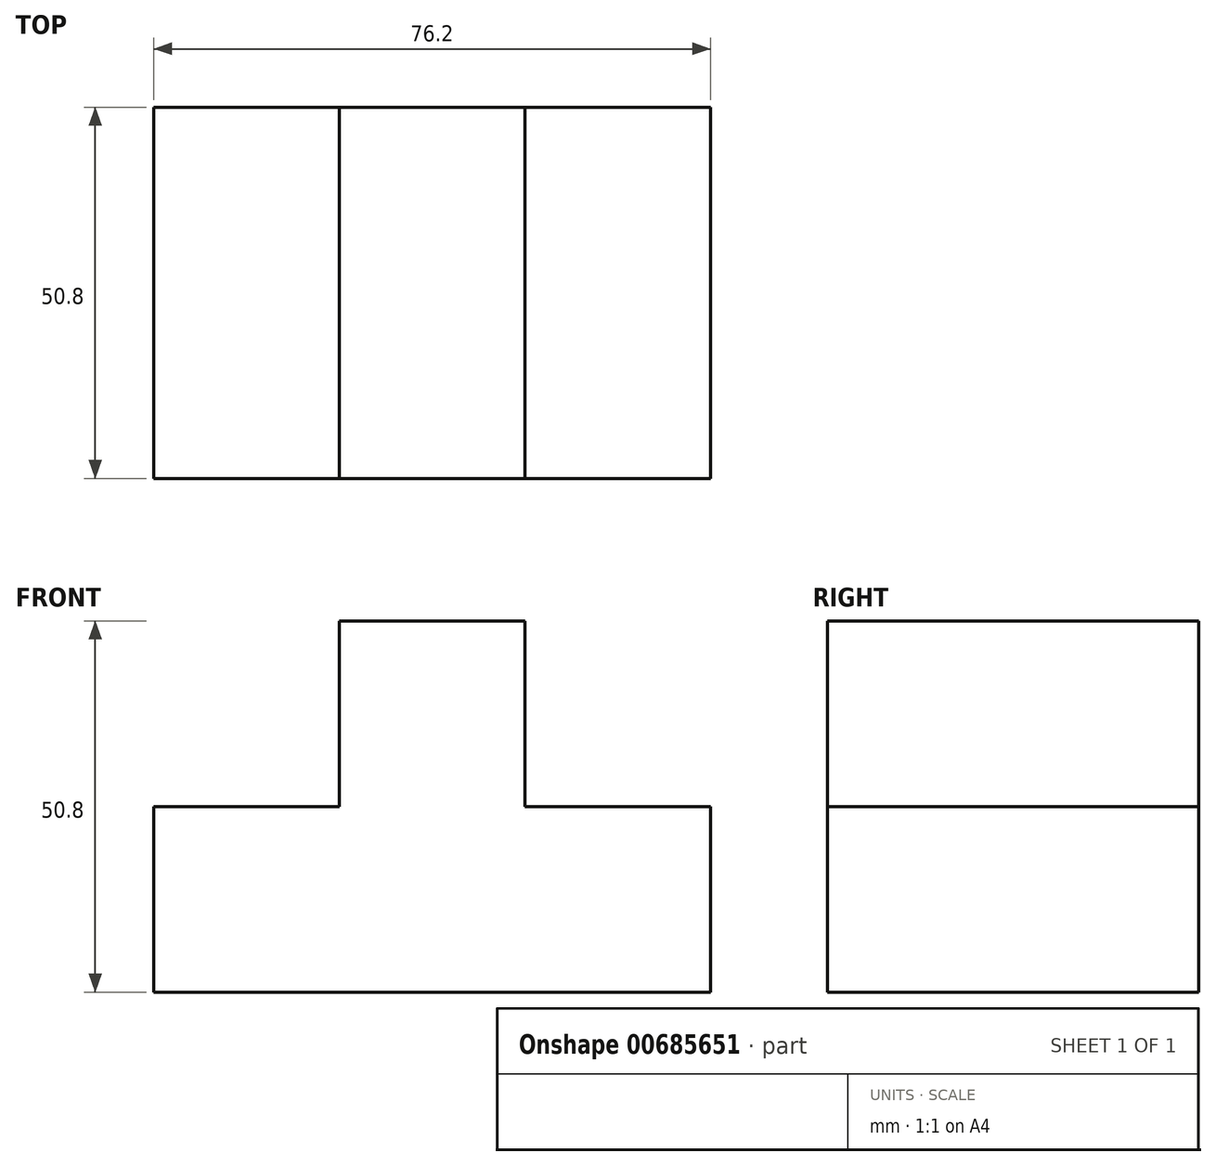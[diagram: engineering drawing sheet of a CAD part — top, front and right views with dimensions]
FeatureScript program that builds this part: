
annotation { "Feature Type Name" : "Feature", "Feature Type Description" : "" }
export const myFeature = defineFeature(function(context is Context, id is Id, definition is map)
    precondition{}
    {
        {
            var Q0;
            Q0=qCreatedBy(makeId("Front.planeOp"),FACE);
            var sketch = newSketch(context, id + "F0", { "sketchPlane" : qUnion([Q0])});
            skLineSegment(sketch, "E0", {"start": v(0, 0) * mm, "end": v(-76.2, 0) * mm});
            skLineSegment(sketch, "E1", {"start": v(-76.2, 0) * mm, "end": v(-76.2, 25.4) * mm});
            skLineSegment(sketch, "E2", {"start": v(0, 0) * mm, "end": v(0, 25.4) * mm});
            skLineSegment(sketch, "E3", {"start": v(-76.2, 25.4) * mm, "end": v(-50.8, 25.4) * mm});
            skLineSegment(sketch, "E4", {"start": v(0, 25.4) * mm, "end": v(-25.4, 25.4) * mm});
            skLineSegment(sketch, "E5", {"start": v(-25.4, 25.4) * mm, "end": v(-25.4, 50.8) * mm});
            skLineSegment(sketch, "E6", {"start": v(-25.4, 50.8) * mm, "end": v(-50.8, 50.8) * mm});
            skLineSegment(sketch, "E7", {"start": v(-50.8, 50.8) * mm, "end": v(-50.8, 25.4) * mm});
            skSolve(sketch);
        }
        {
            var Q0;
            Q0 = qSketchRegion(id + "F0", true);
            extrude(context, id + "F1", {"entities" : qUnion([Q0]), "depth" : 50.8 * mm, "offsetDistance" : 25.4 * mm});
        }
    });
